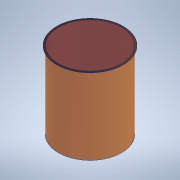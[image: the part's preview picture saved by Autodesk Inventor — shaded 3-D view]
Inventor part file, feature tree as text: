
AUTODESK INVENTOR PART (.ipt)
format: ipt  version: 2021 (Build 250183000, 183)  size: 119,808 bytes
history: native  units: mm
features: thicken_offset x1, sketch x1, other x1, revolve x1
ambient origin geometry x8: Origin, YZ Plane, XZ Plane, XY Plane, X Axis, Y Axis, Z Axis, Center Point
bodies: Solid1 (feature_tree)
feature tree (4):
  thicken_offset  "Thicken1"
  sketch  "Sketch1"  dims[d0=620.0mm d1=255.0mm d2=13.0mm d3=90.0deg d4=2.0mm d5=2.0mm]
  other  "Srf1"
  revolve  "RevolutionSrf1"  [1 undecoded]
note: 1 required parameter value undecoded (feature->parameter linkage not recoverable at this tier; creation-order binding heuristic only, values carry confidence <= 0.55)
